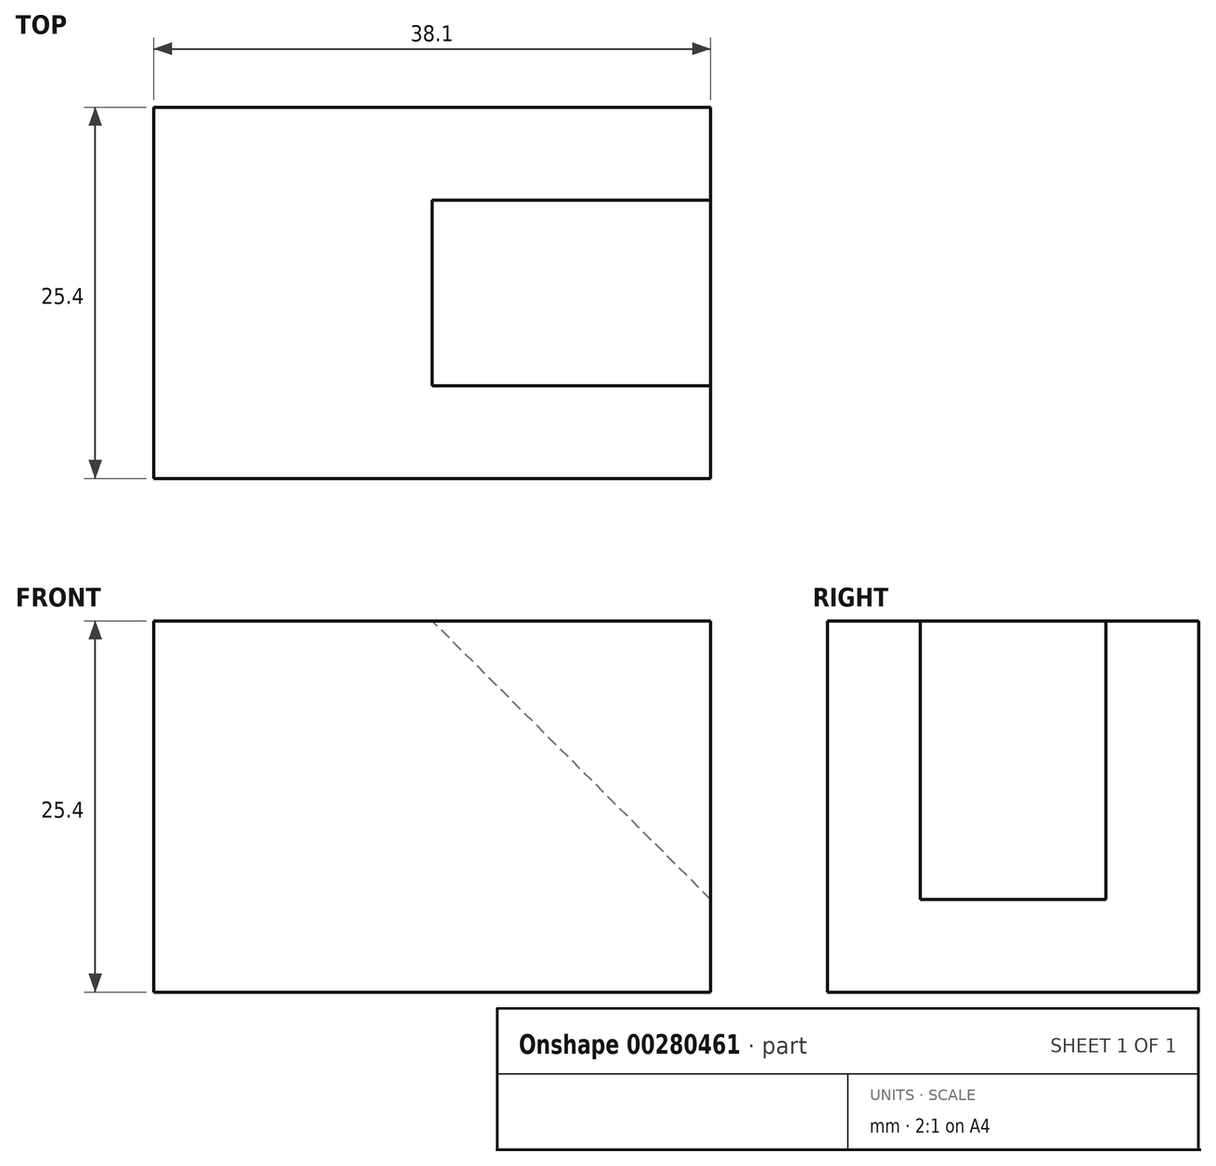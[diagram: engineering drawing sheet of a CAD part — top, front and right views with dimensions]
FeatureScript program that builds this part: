
annotation { "Feature Type Name" : "Feature", "Feature Type Description" : "" }
export const myFeature = defineFeature(function(context is Context, id is Id, definition is map)
    precondition{}
    {
        {
            var Q0;
            Q0=qCreatedBy(makeId("Front.planeOp"),FACE);
            var sketch = newSketch(context, id + "F0", { "sketchPlane" : qUnion([Q0])});
            skLineSegment(sketch, "E0.bottom", {"start": v(0, 0) * mm, "end": v(38.1, 0) * mm});
            skLineSegment(sketch, "E0.top", {"start": v(0, 25.4) * mm, "end": v(38.1, 25.4) * mm});
            skLineSegment(sketch, "E0.left", {"start": v(0, 0) * mm, "end": v(0, 25.4) * mm});
            skLineSegment(sketch, "E0.right", {"start": v(38.1, 0) * mm, "end": v(38.1, 25.4) * mm});
            skSolve(sketch);
        }
        {
            var Q0;
            Q0=makeQuery(id+"F0.imprint","IMPRINT",FACE,{"disambiguationData":[TD([[makeQuery(id+"F0.imprint","IMPRINT",EDGE,{"derivedFrom":sQuery(id+"F0.wireOp",EDGE,"E0.bottom")}),1.0]])]});
            extrude(context, id + "F1", {"entities" : qUnion([Q0]), "endBound" : BoundingType.SYMMETRIC, "depth" : 25.4 * mm});
        }
        {
            var Q0;
            Q0=qCreatedBy(makeId("Front.planeOp"),FACE);
            var sketch = newSketch(context, id + "F2", { "sketchPlane" : qUnion([Q0])});
            skLineSegment(sketch, "E1", {"start": v(19.05, 25.4) * mm, "end": v(38.1, 25.4) * mm});
            skLineSegment(sketch, "E2", {"start": v(38.1, 25.4) * mm, "end": v(38.1, 6.35) * mm});
            skLineSegment(sketch, "E3", {"start": v(38.1, 6.35) * mm, "end": v(19.05, 25.4) * mm});
            skSolve(sketch);
        }
        {
            var Q0;
            Q0 = qSketchRegion(id + "F2", true);
            extrude(context, id + "F3", {"entities" : qUnion([Q0]), "operationType" : NewBodyOperationType.REMOVE, "endBound" : BoundingType.SYMMETRIC, "depth" : 12.7 * mm});
        }
    });
